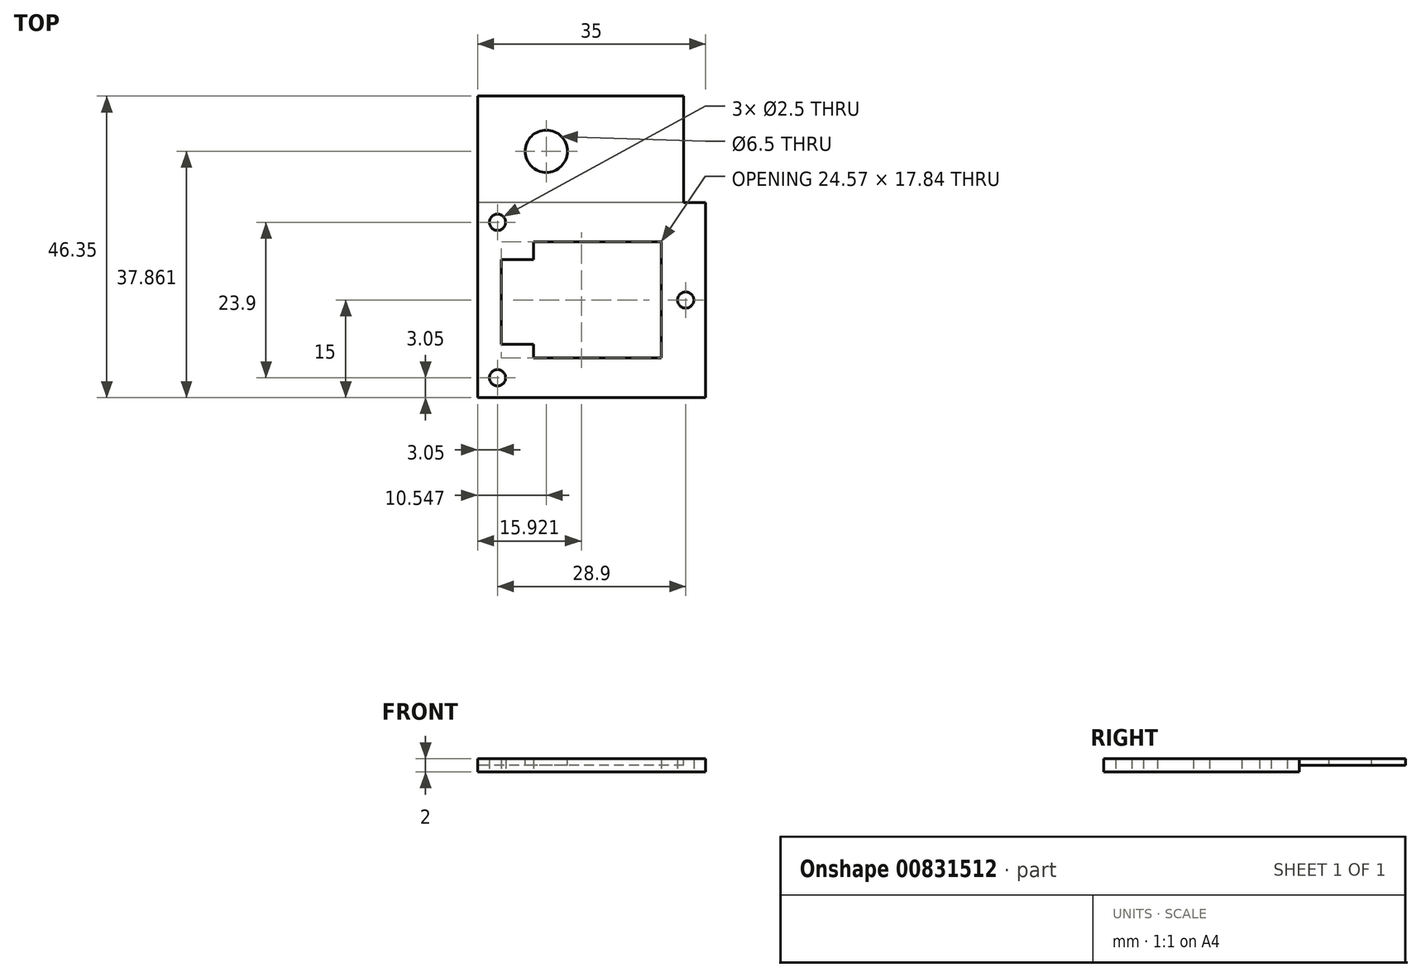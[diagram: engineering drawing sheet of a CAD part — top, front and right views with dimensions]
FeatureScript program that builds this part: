
annotation { "Feature Type Name" : "Feature", "Feature Type Description" : "" }
export const myFeature = defineFeature(function(context is Context, id is Id, definition is map)
    precondition{}
    {
        {
            var Q0;
            Q0=qCreatedBy(makeId("Top.planeOp"),FACE);
            var sketch = newSketch(context, id + "F0", { "sketchPlane" : qUnion([Q0])});
            skLineSegment(sketch, "E0.bottom", {"start": v(17.5, 15) * mm, "end": v(-17.5, 15) * mm});
            skLineSegment(sketch, "E0.top", {"start": v(17.5, -15) * mm, "end": v(-17.5, -15) * mm});
            skLineSegment(sketch, "E0.left", {"start": v(17.5, 15) * mm, "end": v(17.5, -15) * mm});
            skLineSegment(sketch, "E0.right", {"start": v(-17.5, 15) * mm, "end": v(-17.5, -15) * mm});
            skPoint(sketch, "E0.middle", {"position": v(0, 0) * mm});
            skCircle(sketch, "E1", {"center": v(-14.45, 11.95) * mm, "radius": 1.25 * mm});
            skCircle(sketch, "E2", {"center": v(-14.45, -11.95) * mm, "radius": 1.25 * mm});
            skCircle(sketch, "E3", {"center": v(14.45, 0) * mm, "radius": 1.25 * mm});
            skLineSegment(sketch, "E4.bottom", {"start": v(8.92, 8.92) * mm, "end": v(-8.92, 8.92) * mm});
            skLineSegment(sketch, "E4.top", {"start": v(8.92, -8.92) * mm, "end": v(-8.92, -8.92) * mm});
            skLineSegment(sketch, "E4.left", {"start": v(8.92, 8.92) * mm, "end": v(8.92, -8.92) * mm});
            skLineSegment(sketch, "E4.right", {"start": v(-8.92, 8.92) * mm, "end": v(-8.92, -8.92) * mm});
            skLineSegment(sketch, "E5", {"start": v(-8.92, 6.19) * mm, "end": v(-13.86, 6.19) * mm});
            skLineSegment(sketch, "E6", {"start": v(-13.86, 6.19) * mm, "end": v(-13.86, -6.78) * mm});
            skLineSegment(sketch, "E7", {"start": v(-13.86, -6.78) * mm, "end": v(-8.92, -6.78) * mm});
            skLineSegment(sketch, "E8", {"start": v(8.92, 8.92) * mm, "end": v(10.7, 8.92) * mm});
            skLineSegment(sketch, "E9", {"start": v(8.92, -8.92) * mm, "end": v(10.7, -8.92) * mm});
            skLineSegment(sketch, "E10", {"start": v(10.7, 8.92) * mm, "end": v(10.7, -8.92) * mm});
            skSolve(sketch);
        }
        {
            var Q0;
            Q0=qSketchRegion(id+"F0",true);
            extrude(context, id + "F1", {"entities" : qUnion([Q0]), "depth" : 2 * mm, "offsetDistance" : 25.4 * mm});
        }
        {
            var Q0;
            Q0=makeQuery(id+"F1.opExtrude","CAP_FACE",FACE,{"disambiguationData":[OSD([sQuery(id+"F0.wireOp",EDGE,"E0.bottom"),sQuery(id+"F0.wireOp",EDGE,"E0.top"),sQuery(id+"F0.wireOp",EDGE,"E0.left"),sQuery(id+"F0.wireOp",EDGE,"E0.right"),sQuery(id+"F0.wireOp",EDGE,"E1"),sQuery(id+"F0.wireOp",EDGE,"E2"),sQuery(id+"F0.wireOp",EDGE,"E3"),sQuery(id+"F0.wireOp",EDGE,"E4.bottom"),sQuery(id+"F0.wireOp",EDGE,"E4.top"),sQuery(id+"F0.wireOp",EDGE,"E4.right"),sQuery(id+"F0.wireOp",EDGE,"E5"),sQuery(id+"F0.wireOp",EDGE,"E6"),sQuery(id+"F0.wireOp",EDGE,"E7"),sQuery(id+"F0.wireOp",EDGE,"E8"),sQuery(id+"F0.wireOp",EDGE,"E9"),sQuery(id+"F0.wireOp",EDGE,"E10")])],"isStart":false});
            var sketch = newSketch(context, id + "F2", { "sketchPlane" : qUnion([Q0])});
            skLineSegment(sketch, "E11.bottom", {"start": v(-17.5, 15) * mm, "end": v(14.16, 15) * mm});
            skLineSegment(sketch, "E11.top", {"start": v(-17.5, 31.35) * mm, "end": v(14.16, 31.35) * mm});
            skLineSegment(sketch, "E11.left", {"start": v(-17.5, 15) * mm, "end": v(-17.5, 31.35) * mm});
            skLineSegment(sketch, "E11.right", {"start": v(14.16, 15) * mm, "end": v(14.16, 31.35) * mm});
            skCircle(sketch, "E12", {"center": v(-6.95, 22.86) * mm, "radius": 3.25 * mm});
            skSolve(sketch);
        }
        {
            var Q0;
            Q0 = qSketchRegion(id + "F2", true);
            extrude(context, id + "F3", {"entities" : qUnion([Q0]), "operationType" : NewBodyOperationType.ADD, "oppositeDirection" : true, "depth" : 1 * mm, "offsetDistance" : 25.4 * mm});
        }
    });
